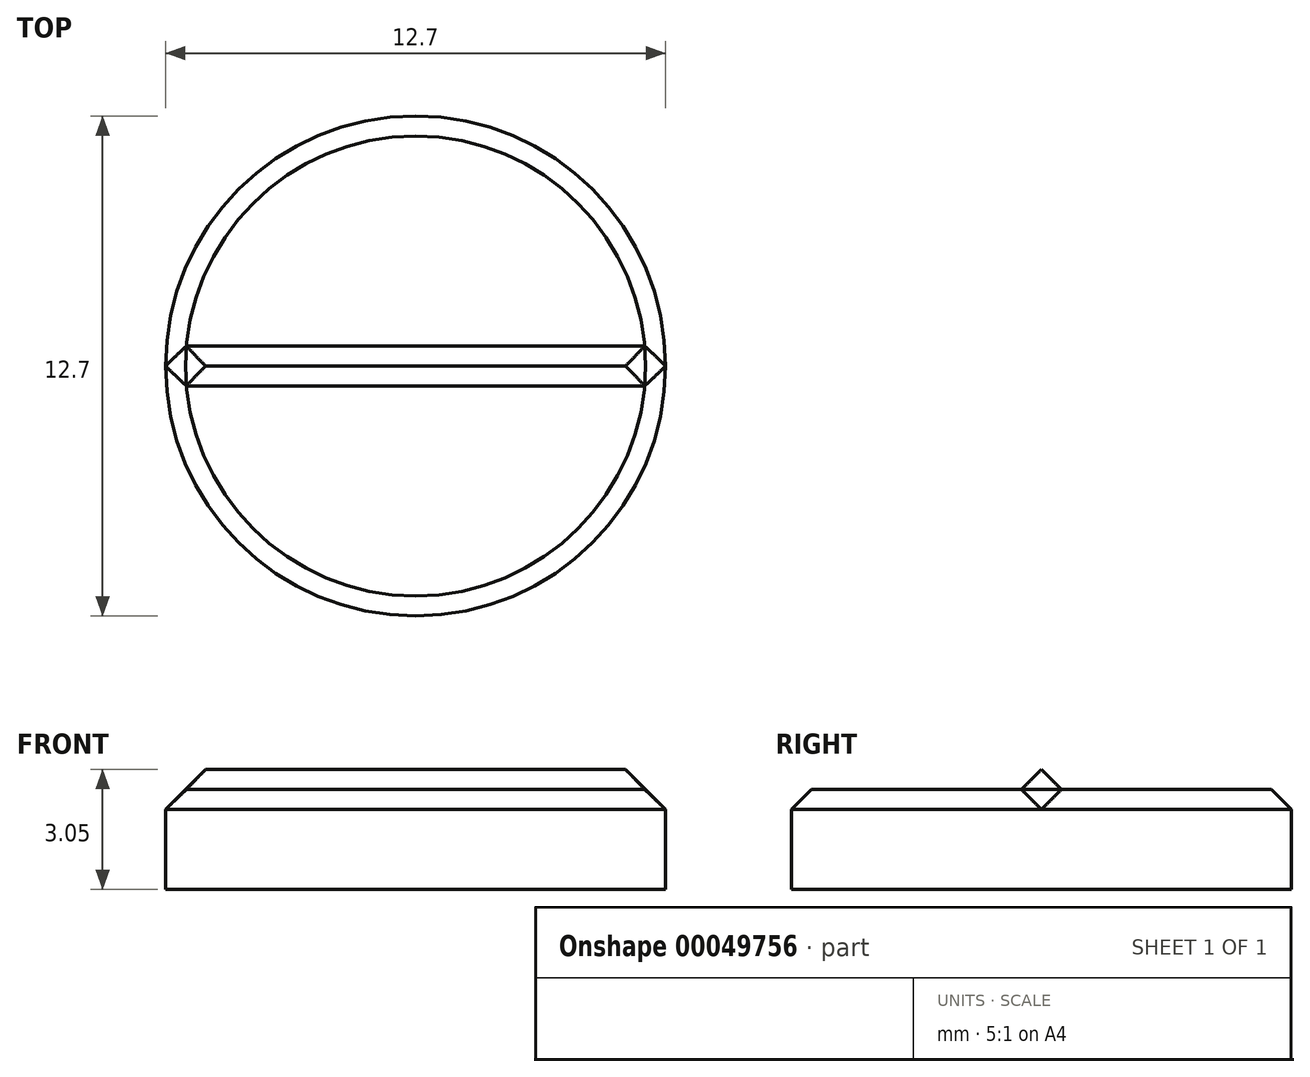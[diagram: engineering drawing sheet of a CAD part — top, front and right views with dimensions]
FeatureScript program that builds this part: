
annotation { "Feature Type Name" : "Feature", "Feature Type Description" : "" }
export const myFeature = defineFeature(function(context is Context, id is Id, definition is map)
    precondition{}
    {
        {
            var Q0;
            Q0=qCreatedBy(makeId("Top.planeOp"),FACE);
            var sketch = newSketch(context, id + "F0", { "sketchPlane" : qUnion([Q0])});
            skCircle(sketch, "E0", {"center": v(0, 0) * mm, "radius": 6.35 * mm});
            skSolve(sketch);
        }
        {
            var Q0;
            Q0=qCreatedBy(makeId("Top.planeOp"),FACE);
            var sketch = newSketch(context, id + "F1", { "sketchPlane" : qUnion([Q0])});
            skCircle(sketch, "E1", {"center": v(0, 0) * mm, "radius": 1.27 * mm});
            skSolve(sketch);
        }
        {
            var Q0;
            Q0=qCreatedBy(makeId("Right.planeOp"),FACE);
            var sketch = newSketch(context, id + "F2", { "sketchPlane" : qUnion([Q0])});
            skCircle(sketch, "E2.cCircle", {"center": v(0, 0) * mm, "radius": 0.5 * mm, "construction": true});
            skLineSegment(sketch, "E2.0", {"start": v(0.5, 0) * mm, "end": v(0, -0.5) * mm});
            skLineSegment(sketch, "E2.1", {"start": v(0, -0.5) * mm, "end": v(-0.5, 0) * mm});
            skLineSegment(sketch, "E2.2", {"start": v(-0.5, 0) * mm, "end": v(0, 0.5) * mm});
            skLineSegment(sketch, "E2.3", {"start": v(0, 0.5) * mm, "end": v(0.5, 0) * mm});
            skLineSegment(sketch, "E3", {"start": v(0, 0) * mm, "end": v(0, -0.5) * mm});
            skSolve(sketch);
        }
        {
            var Q0;
            Q0=qSketchRegion(id+"F2",true);
            extrude(context, id + "F3", {"entities" : qUnion([Q0]), "endBound" : BoundingType.SYMMETRIC, "oppositeDirection" : true, "depth" : 12.7 * mm});
        }
        {
            var Q0;
            Q0=qSketchRegion(id+"F0",true);
            extrude(context, id + "F4", {"entities" : qUnion([Q0]), "oppositeDirection" : true, "depth" : 2.54 * mm});
        }
        {
            var Q0;
            Q0=makeQuery(id+"F0.imprint","IMPRINT",FACE,{"disambiguationData":[TD([[makeQuery(id+"F0.imprint","IMPRINT",EDGE,{"derivedFrom":sQuery(id+"F0.wireOp",EDGE,"E0")}),1.0]])]});
            var sketch = newSketch(context, id + "F5", { "sketchPlane" : qUnion([Q0])});
            skCircle(sketch, "E4", {"center": v(0, 0) * mm, "radius": 12.7 * mm});
            skCircle(sketch, "E5", {"center": v(0, 0) * mm, "radius": 6.35 * mm});
            skSolve(sketch);
        }
        {
            var Q0;
            Q0=qSketchRegion(id+"F5",true);
            extrude(context, id + "F6", {"entities" : qUnion([Q0]), "operationType" : NewBodyOperationType.REMOVE, "endBound" : BoundingType.SYMMETRIC, "depth" : 12.7 * mm});
        }
        {
            var Q0;
            Q0=qCreatedBy(makeId("Front.planeOp"),FACE);
            var sketch = newSketch(context, id + "F7", { "sketchPlane" : qUnion([Q0])});
            skCircle(sketch, "E6.cCircle", {"center": v(5.84, 0) * mm, "radius": 0.72 * mm, "construction": true});
            skLineSegment(sketch, "E6.0", {"start": v(5.33, 0.5) * mm, "end": v(6.35, 0.5) * mm});
            skLineSegment(sketch, "E6.1", {"start": v(6.35, 0.5) * mm, "end": v(6.35, -0.5) * mm});
            skLineSegment(sketch, "E6.2", {"start": v(6.35, -0.5) * mm, "end": v(5.33, 0.5) * mm});
            skSolve(sketch);
        }
        {
            var Q0;
            Q0 = qSketchRegion(id + "F7", true);
            var Q1;
            Q1=sQuery(id+"F2.wireOp",EDGE,"E3");
            revolve(context, id + "F8", {"operationType" : NewBodyOperationType.REMOVE, "entities" : qUnion([Q0]), "axis" : qUnion([Q1]), "revolveType" : RevolveType.FULL});
        }
    });
